# Revit family: Single Handle Lavatory Faucet without pop-up waste_TOTO_TLG04306
name_source: partatom
category: 衛生器具
revit_build: Autodesk Revit 2018 (Build: 20181011_1500(x64)
units: mm (PartAtom-declared; Revit-internal decimal feet)

## family parameters
OmniClass タイトル = Sanitary, Laundry, and Cleaning Equipment
OmniClass 番号 = 23.45.00.00
パーツ タイプ = 標準
ロード時にボイドで切り取り = いいえ
丸型コネクタ寸法 = 直径を使用
作業面ベース = いいえ
共有 = いいえ
常に垂直 = はい
部屋計算ポイント = いいえ

## types (1)
- Single Handle Lavatory Faucet without pop-up waste_TOTO_TLG04306
    Finish = faucet_material
    Height = 210  [stored 0.688976 ft]
    Length = 170
    TOTO AsiaOceania = TLG04306B
    TOTO AsiaOceania URL = http://asia.toto.com
    TOTO China = TLG04306B
    TOTO China URL = http://www.toto.com.cn
    TOTO India = TLG04306B
    TOTO India URL = https://in.toto.com
    TOTO Taiwan = TLG04306PAR
    TOTO Taiwan URL = https://www.twtoto.com.tw
    Width = 48
    タイプの説明 = for Semi-tall Vessel
    モデル = TLG04306
    製造元 = TOTO Ltd.
    説明 = Single Handle Lavatory Faucet without pop-up waste/单柄双控洗面器水嘴

note: [stored X ft] marks values corroborated as IEEE doubles in the binary element streams (Revit-internal decimal feet)

## geometry (parser evidence)
native form markers: Blend x2, Sweep x1
no freeform markers — native parametric forms only
